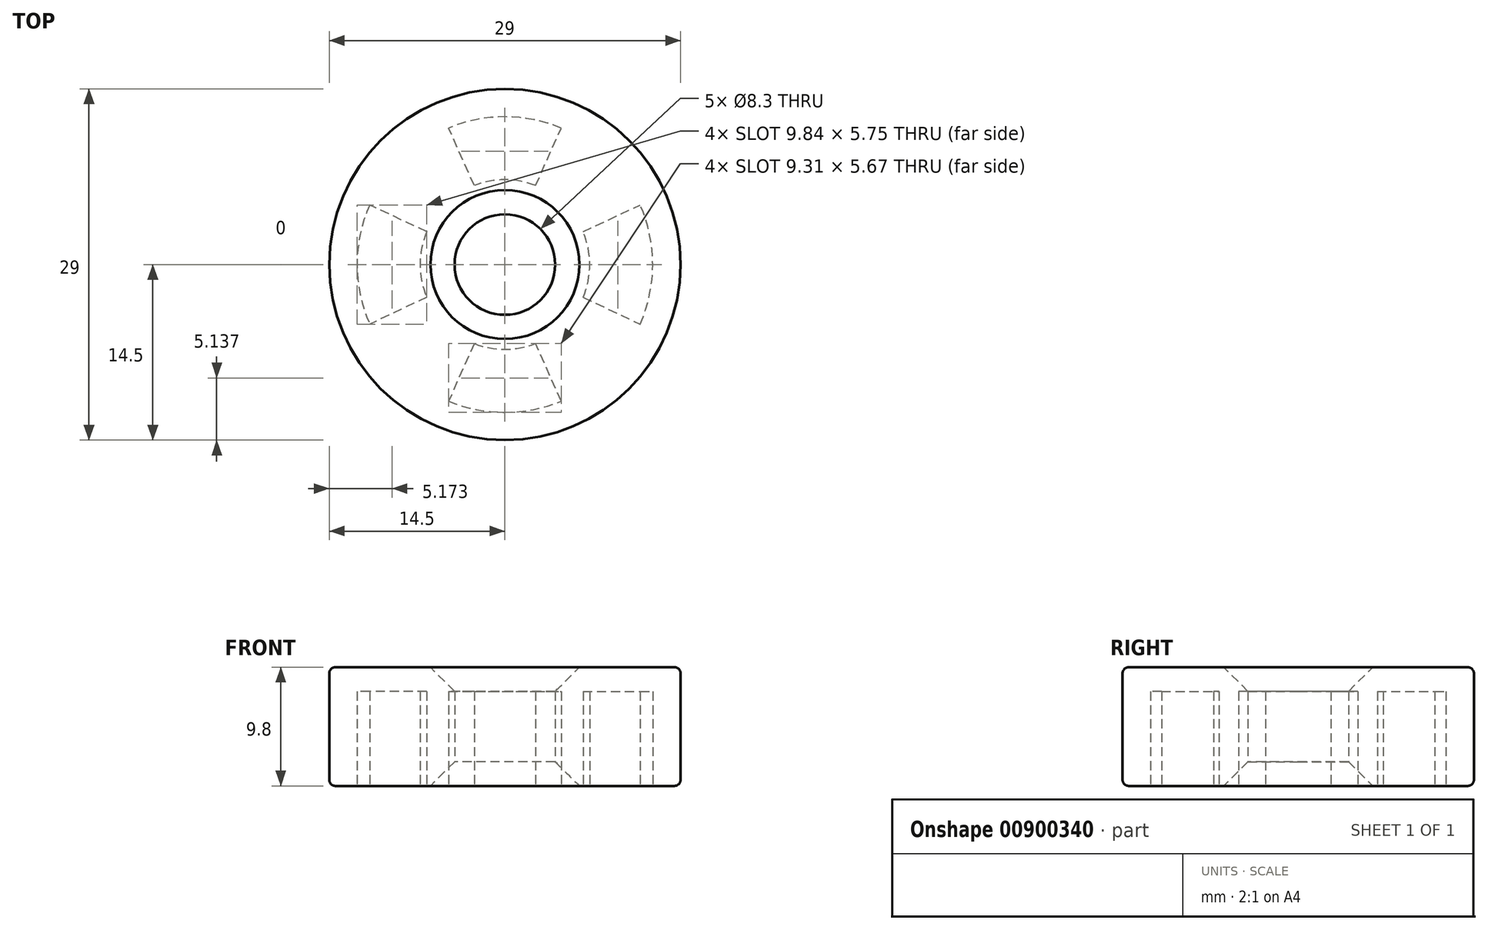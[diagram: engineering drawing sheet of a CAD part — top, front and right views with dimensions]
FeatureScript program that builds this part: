
annotation { "Feature Type Name" : "Feature", "Feature Type Description" : "" }
export const myFeature = defineFeature(function(context is Context, id is Id, definition is map)
    precondition{}
    {
        {
            var Q0;
            Q0=qCreatedBy(makeId("Top.planeOp"),FACE);
            var sketch = newSketch(context, id + "F0", { "sketchPlane" : qUnion([Q0])});
            skCircle(sketch, "E0", {"center": v(0, 0) * mm, "radius": 14.5 * mm});
            skCircle(sketch, "E1", {"center": v(0, 0) * mm, "radius": 4.15 * mm});
            skSolve(sketch);
        }
        {
            var Q0;
            Q0 = qSketchRegion(id + "F0", true);
            extrude(context, id + "F1", {"entities" : qUnion([Q0]), "depth" : 9.8 * mm, "offsetDistance" : 25 * mm});
        }
        {
            var Q0;
            Q0=makeQuery(id+"F1.opExtrude","CAP_EDGE",EDGE,{"disambiguationData":[OSD([sQuery(id+"F0.wireOp",EDGE,"E1")])],"isStart":false});
            var Q1;
            Q1=makeQuery(id+"F1.opExtrude","CAP_EDGE",EDGE,{"disambiguationData":[OSD([sQuery(id+"F0.wireOp",EDGE,"E1")])],"isStart":true});
            chamfer(context, id + "F2", {"entities" : qUnion([Q0, Q1]), "width" : 2 * mm, "tangentPropagation" : true});
        }
        {
            var Q0;
            Q0=makeQuery(id+"F1.opExtrude","CAP_FACE",FACE,{"disambiguationData":[OSD([sQuery(id+"F0.wireOp",EDGE,"E0"),sQuery(id+"F0.wireOp",EDGE,"E1")])],"isStart":true});
            var sketch = newSketch(context, id + "F3", { "sketchPlane" : qUnion([Q0])});
            skArc(sketch, "E2", {"start": v(-11.16, 4.92) * mm, "mid": v(-12.2, 0) * mm, "end": v(-11.16, -4.92) * mm});
            skArc(sketch, "E3", {"start": v(-6.45, 2.71) * mm, "mid": v(-7, 0) * mm, "end": v(-6.45, -2.71) * mm});
            skLineSegment(sketch, "E4", {"start": v(4.65, 11.28) * mm, "end": v(2.53, 6.53) * mm});
            skLineSegment(sketch, "E5", {"start": v(-2.53, 6.53) * mm, "end": v(-4.65, 11.28) * mm});
            skLineSegment(sketch, "E6", {"start": v(2.53, -6.53) * mm, "end": v(4.65, -11.28) * mm});
            skLineSegment(sketch, "E7", {"start": v(-2.53, -6.53) * mm, "end": v(-4.65, -11.28) * mm});
            skLineSegment(sketch, "E8", {"start": v(-6.45, 2.71) * mm, "end": v(-11.16, 4.92) * mm});
            skLineSegment(sketch, "E9", {"start": v(-6.45, -2.71) * mm, "end": v(-11.16, -4.92) * mm});
            skLineSegment(sketch, "E10", {"start": v(6.45, 2.71) * mm, "end": v(11.16, 4.92) * mm});
            skLineSegment(sketch, "E11", {"start": v(6.45, -2.71) * mm, "end": v(11.16, -4.92) * mm});
            skArc(sketch, "E12.trimOffspring", {"start": v(-2.53, -6.53) * mm, "mid": v(0, -7) * mm, "end": v(2.53, -6.53) * mm});
            skArc(sketch, "E13.trimOffspring", {"start": v(-4.65, -11.28) * mm, "mid": v(0, -12.2) * mm, "end": v(4.65, -11.28) * mm});
            skArc(sketch, "E14.trimOffspring", {"start": v(11.16, -4.92) * mm, "mid": v(12.2, 0) * mm, "end": v(11.16, 4.92) * mm});
            skArc(sketch, "E15.trimOffspring", {"start": v(6.45, -2.71) * mm, "mid": v(7, 0) * mm, "end": v(6.45, 2.71) * mm});
            skArc(sketch, "E16.trimOffspring", {"start": v(4.65, 11.28) * mm, "mid": v(0, 12.2) * mm, "end": v(-4.65, 11.28) * mm});
            skArc(sketch, "E17.trimOffspring", {"start": v(2.53, 6.53) * mm, "mid": v(0, 7) * mm, "end": v(-2.53, 6.53) * mm});
            skSolve(sketch);
        }
        {
            var Q0;
            Q0=makeQuery(id+"F3.imprint","IMPRINT",FACE,{"disambiguationData":[TD([[makeQuery(id+"F3.imprint","IMPRINT",EDGE,{"derivedFrom":sQuery(id+"F3.wireOp",EDGE,"E4")}),-1.0]])]});
            var Q1;
            Q1=makeQuery(id+"F3.imprint","IMPRINT",FACE,{"disambiguationData":[TD([[makeQuery(id+"F3.imprint","IMPRINT",EDGE,{"derivedFrom":sQuery(id+"F3.wireOp",EDGE,"E2")}),1.0]])]});
            var Q2;
            Q2=makeQuery(id+"F3.imprint","IMPRINT",FACE,{"disambiguationData":[TD([[makeQuery(id+"F3.imprint","IMPRINT",EDGE,{"derivedFrom":sQuery(id+"F3.wireOp",EDGE,"E6")}),-1.0]])]});
            var Q3;
            Q3=makeQuery(id+"F3.imprint","IMPRINT",FACE,{"disambiguationData":[TD([[makeQuery(id+"F3.imprint","IMPRINT",EDGE,{"derivedFrom":sQuery(id+"F3.wireOp",EDGE,"E10")}),-1.0]])]});
            extrude(context, id + "F4", {"entities" : qUnion([Q0, Q1, Q2, Q3]), "operationType" : NewBodyOperationType.REMOVE, "oppositeDirection" : true, "depth" : 7.8 * mm, "offsetDistance" : 25 * mm});
        }
        {
            var Q0;
            Q0=makeQuery(id+"F1.opExtrude","CAP_EDGE",EDGE,{"disambiguationData":[OSD([sQuery(id+"F0.wireOp",EDGE,"E0")])],"isStart":false});
            var Q1;
            Q1=makeQuery(id+"F1.opExtrude","CAP_EDGE",EDGE,{"disambiguationData":[OSD([sQuery(id+"F0.wireOp",EDGE,"E0")])],"isStart":true});
            fillet(context, id + "F5", {"entities" : qUnion([Q0, Q1]), "radius" : 0.5 * mm, "tangentPropagation" : true, "allowEdgeOverflow" : false});
        }
    });
